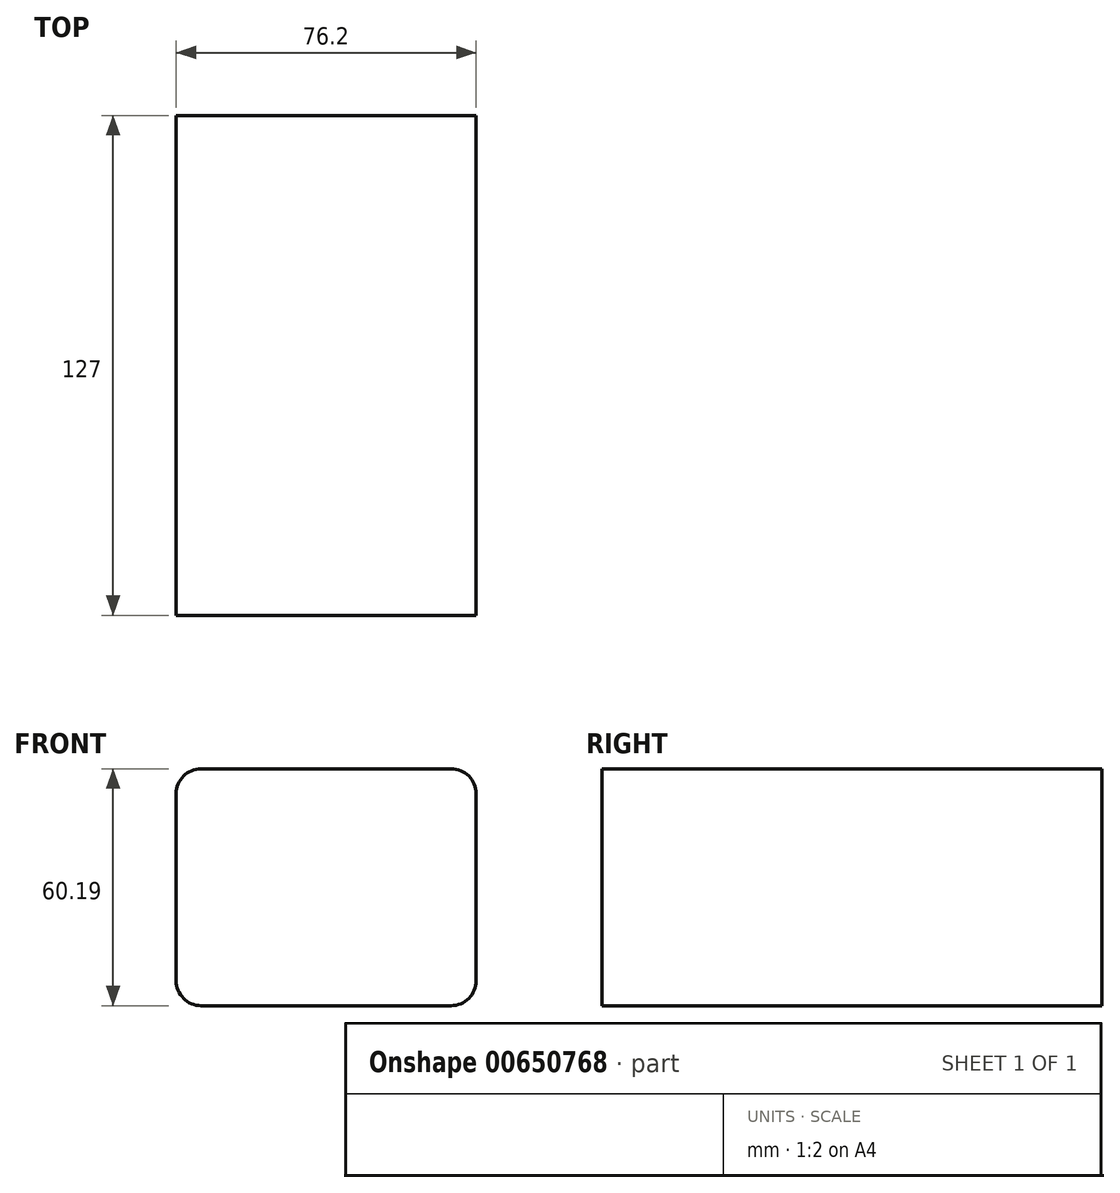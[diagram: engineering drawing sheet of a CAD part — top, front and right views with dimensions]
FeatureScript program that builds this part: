
annotation { "Feature Type Name" : "Feature", "Feature Type Description" : "" }
export const myFeature = defineFeature(function(context is Context, id is Id, definition is map)
    precondition{}
    {
        {
            var Q0;
            Q0=qCreatedBy(makeId("Front.planeOp"),FACE);
            var sketch = newSketch(context, id + "F0", { "sketchPlane" : qUnion([Q0])});
            skLineSegment(sketch, "E0.bottom", {"start": v(-6.35, 0) * mm, "end": v(-69.85, 0) * mm});
            skLineSegment(sketch, "E0.top", {"start": v(-6.35, 60.2) * mm, "end": v(-69.85, 60.2) * mm});
            skLineSegment(sketch, "E0.left", {"start": v(0, 6.35) * mm, "end": v(0, 53.84) * mm});
            skLineSegment(sketch, "E0.right", {"start": v(-76.2, 6.35) * mm, "end": v(-76.2, 53.84) * mm});
            skPoint(sketch, "E1.visualSharp", {"position": v(-76.2, 60.2) * mm});
            skArc(sketch, "E1.filletArc", {"start": v(-69.85, 60.2) * mm, "mid": v(-74.34, 58.33) * mm, "end": v(-76.2, 53.84) * mm});
            skPoint(sketch, "E2.visualSharp", {"position": v(-76.2, 0) * mm});
            skArc(sketch, "E2.filletArc", {"start": v(-76.2, 6.35) * mm, "mid": v(-74.34, 1.86) * mm, "end": v(-69.85, 0) * mm});
            skPoint(sketch, "E3.visualSharp", {"position": v(0, 0) * mm});
            skArc(sketch, "E3.filletArc", {"start": v(-6.35, 0) * mm, "mid": v(-1.86, 1.86) * mm, "end": v(0, 6.35) * mm});
            skPoint(sketch, "E4.visualSharp", {"position": v(0, 60.2) * mm});
            skArc(sketch, "E4.filletArc", {"start": v(0, 53.84) * mm, "mid": v(-1.86, 58.33) * mm, "end": v(-6.35, 60.2) * mm});
            skSolve(sketch);
        }
        {
            var Q0;
            Q0 = qSketchRegion(id + "F0", true);
            extrude(context, id + "F1", {"entities" : qUnion([Q0]), "endBound" : BoundingType.SYMMETRIC, "depth" : 127 * mm, "offsetDistance" : 25.4 * mm});
        }
    });
